# Revit family: Faucet-Lavatory-KOHLER-KUMIN-K-98827T_1
name_source: partatom
category: Plumbing Fixtures
revit_build: Autodesk Revit 2017 (Build: 20160225_1515(x64)
units: mm (PartAtom-declared; Revit-internal decimal feet)

## family parameters
Cut with Voids When Loaded = No
Host = Face
OmniClass Number = 23.31.11.00
Part Type = Normal
Room Calculation Point = No
Round Connector Dimension = Use Diameter
Shared = No

## types (6) — shared parameters
ADA Compliant = No
Assembly Code = D2010
CW Connection = Yes
Cold Water Inlet = Cold Water Inlet
Date Modified = 08/24/2020
Default Elevation = 36"
Finish = Kohler-Metal-CP-Polished_Chrome
HW Connection = Yes
Handle Clearance = 3 3/16"
Height = 6 3/8"
Hot Water Inlet = Hot Water Inlet
Length = 3 7/8"
Manufacturer = KOHLER Co.
Master Format 2014 = 22 41 39
Master Format 2014 Name = Residential Faucets, Supplies, and Trim
Material = Premium Metal construction
Product Name = KUMIN
Spout Reach = 3 7/8"
URL = http://www.kohler.com.cn
Vent Connection = No
Waste Connection = No
Waste Water Outlet = Waste Water Outlet
WaterSense Certified = No
Width = 1 7/8"

## per-type parameters (varying)
| type | 2 Connectors | Description | Dist | Drain Included | Flow Rate | Hot Water Connector Diameter | Indicators | Model | Pressure | Product Documentation Link | Product Page URL | Type |
| CP-Polished Chrome | Yes | Single handle basin mixer | 3/8" | Yes | 0 GPM | 1/2" | Yes | K-98827T-4-CP | 0.00 psi | https://files.kohler.com.cn | https://www.kohler.com.cn | 1 |
| Cold only, 1.5 GPM, CP-Polished Chrome | No | Cold water lavatory faucet | 0" | Yes | 2 GPM | 0" | No | K-98827T-4CD-CP | 45.00 psi |  |  | 2 |
| Cold only, 1.2 GPM, CP-Polished Chrome | No | Cold water lavatory faucet | 0" | Yes | 1 GPM | 0" | No | K-98827T-4CD2-CP | 45.00 psi |  |  | 3 |
| Cold Only, CP-Polished Chrome | No | Cold water lavatory faucet | 0" | Yes | 0 GPM | 0" | No | K-98827T-4CDE-CP | 0.00 psi |  |  | 4 |
| 4E2, CP-Polished Chrome | Yes | Single control lavatory faucet | 3/8" | Yes | 0 GPM | 1/2" | Yes | K-98827T-4E2-CP | 0.00 psi |  |  | 5 |
| Without Drain, CP-Polished Chrome | Yes | Single lever lavatory faucet without drain | 3/8" | No | 2 GPM | 1/2" | Yes | K-98827T-4ND-CP | 45.00 psi |  |  | 6 |

## geometry (parser evidence)
native form markers: Sweep x5
no freeform markers — native parametric forms only
